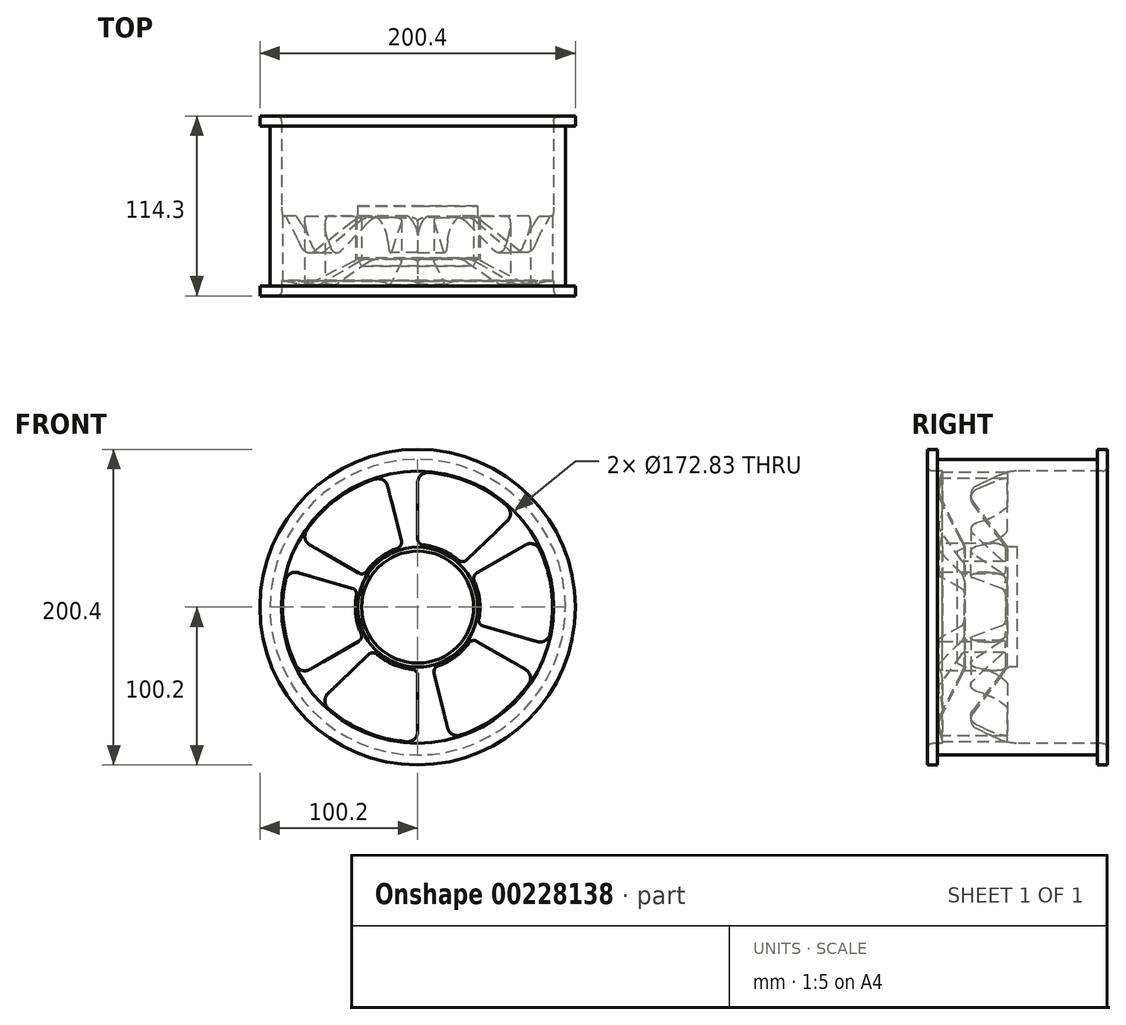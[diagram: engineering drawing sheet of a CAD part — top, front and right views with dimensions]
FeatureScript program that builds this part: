
annotation { "Feature Type Name" : "Feature", "Feature Type Description" : "" }
export const myFeature = defineFeature(function(context is Context, id is Id, definition is map)
    precondition{}
    {
        {
            var Q0;
            Q0=qCreatedBy(makeId("Right.planeOp"),FACE);
            var sketch = newSketch(context, id + "F0", { "sketchPlane" : qUnion([Q0])});
            skLineSegment(sketch, "E0", {"start": v(0, 0) * mm, "end": v(33.02, 0) * mm});
            skLineSegment(sketch, "E1", {"start": v(33.02, 0) * mm, "end": v(33.02, 38.1) * mm});
            skLineSegment(sketch, "E2", {"start": v(33.02, 38.1) * mm, "end": v(27.46, 38.1) * mm});
            skLineSegment(sketch, "E3", {"start": v(26.2, 38.73) * mm, "end": v(4.65, 67.46) * mm});
            skLineSegment(sketch, "E4", {"start": v(6.99, 77) * mm, "end": v(21.47, 83.93) * mm});
            skLineSegment(sketch, "E5", {"start": v(32.43, 86.42) * mm, "end": v(87, 86.42) * mm});
            skLineSegment(sketch, "E6", {"start": v(90.17, 89.6) * mm, "end": v(90.17, 100.2) * mm});
            skLineSegment(sketch, "E7", {"start": v(90.17, 100.2) * mm, "end": v(83.82, 100.2) * mm});
            skLineSegment(sketch, "E8", {"start": v(83.82, 100.2) * mm, "end": v(83.82, 93.85) * mm});
            skLineSegment(sketch, "E9", {"start": v(83.82, 93.85) * mm, "end": v(-17.78, 93.85) * mm});
            skLineSegment(sketch, "E10", {"start": v(-17.78, 93.85) * mm, "end": v(-17.78, 100.2) * mm});
            skLineSegment(sketch, "E11", {"start": v(-17.78, 100.2) * mm, "end": v(-24.13, 100.2) * mm});
            skLineSegment(sketch, "E12", {"start": v(-24.13, 100.2) * mm, "end": v(-24.13, 89.6) * mm});
            skLineSegment(sketch, "E13", {"start": v(-20.95, 86.42) * mm, "end": v(-14.5, 86.42) * mm});
            skLineSegment(sketch, "E14", {"start": v(-14.5, 86.42) * mm, "end": v(-16.6, 78.26) * mm});
            skLineSegment(sketch, "E15", {"start": v(-15.66, 69.41) * mm, "end": v(0, 38.1) * mm});
            skLineSegment(sketch, "E16", {"start": v(0, 38.1) * mm, "end": v(-5.08, 35.56) * mm});
            skLineSegment(sketch, "E17", {"start": v(-5.08, 35.56) * mm, "end": v(-5.08, 0) * mm});
            skLineSegment(sketch, "E18", {"start": v(-5.08, 0) * mm, "end": v(0, 0) * mm});
            skPoint(sketch, "E19.visualSharp", {"position": v(0, 73.66) * mm});
            skArc(sketch, "E19.filletArc", {"start": v(6.99, 77) * mm, "mid": v(3.56, 72.79) * mm, "end": v(4.65, 67.46) * mm});
            skPoint(sketch, "E20.visualSharp", {"position": v(26.67, 86.42) * mm});
            skArc(sketch, "E20.filletArc", {"start": v(32.43, 86.42) * mm, "mid": v(26.81, 85.79) * mm, "end": v(21.47, 83.93) * mm});
            skPoint(sketch, "E21.visualSharp", {"position": v(-17.78, 73.66) * mm});
            skArc(sketch, "E21.filletArc", {"start": v(-16.6, 78.26) * mm, "mid": v(-16.92, 73.75) * mm, "end": v(-15.66, 69.41) * mm});
            skPoint(sketch, "E22.visualSharp", {"position": v(90.17, 86.42) * mm});
            skArc(sketch, "E22.filletArc", {"start": v(87, 86.42) * mm, "mid": v(89.24, 87.35) * mm, "end": v(90.17, 89.6) * mm});
            skPoint(sketch, "E23.visualSharp", {"position": v(-24.13, 86.42) * mm});
            skArc(sketch, "E23.filletArc", {"start": v(-24.13, 89.6) * mm, "mid": v(-23.2, 87.35) * mm, "end": v(-20.95, 86.42) * mm});
            skPoint(sketch, "E24.visualSharp", {"position": v(26.67, 38.1) * mm});
            skArc(sketch, "E24.filletArc", {"start": v(26.2, 38.73) * mm, "mid": v(26.75, 38.27) * mm, "end": v(27.46, 38.1) * mm});
            skSolve(sketch);
        }
        {
            var Q0;
            Q0=makeQuery(id+"F0.imprint","IMPRINT",FACE,{"disambiguationData":[TD([[makeQuery(id+"F0.imprint","IMPRINT",EDGE,{"derivedFrom":sQuery(id+"F0.wireOp",EDGE,"E0")}),1.0]])]});
            var Q1;
            Q1=sQuery(id+"F0.wireOp",EDGE,"E0");
            revolve(context, id + "F1", {"entities" : qUnion([Q0]), "axis" : qUnion([Q1]), "revolveType" : RevolveType.FULL});
        }
        {
            var Q0;
            Q0=makeQuery(id+"F1.opRevolve","SWEPT_FACE",FACE,{"disambiguationData":[OSD([sQuery(id+"F0.wireOp",EDGE,"E17")])]});
            var sketch = newSketch(context, id + "F2", { "sketchPlane" : qUnion([Q0])});
            skArc(sketch, "E25", {"start": v(56.8, 64.21) * mm, "mid": v(33.55, 78.89) * mm, "end": v(6.86, 85.45) * mm});
            skArc(sketch, "E26", {"start": v(25.97, 29.83) * mm, "mid": v(15.47, 36.43) * mm, "end": v(3.45, 39.5) * mm});
            skLineSegment(sketch, "E27", {"start": v(0, 43.29) * mm, "end": v(0, 79.12) * mm});
            skLineSegment(sketch, "E28", {"start": v(31.11, 29.96) * mm, "end": v(57, 54.88) * mm});
            skLineSegment(sketch, "E29.1.0", {"start": v(-10.4, 41.93) * mm, "end": v(-19.04, 76.8) * mm});
            skArc(sketch, "E29.1.1", {"start": v(-12.85, 37.4) * mm, "mid": v(-23.81, 31.6) * mm, "end": v(-32.48, 22.74) * mm});
            skLineSegment(sketch, "E29.1.2", {"start": v(-37.49, 21.64) * mm, "end": v(-68.52, 39.56) * mm});
            skLineSegment(sketch, "E29.2.0", {"start": v(-41.5, 11.96) * mm, "end": v(-76.03, 21.91) * mm});
            skArc(sketch, "E29.2.1", {"start": v(-38.82, 7.57) * mm, "mid": v(-39.28, -4.82) * mm, "end": v(-35.93, -16.76) * mm});
            skLineSegment(sketch, "E29.2.2", {"start": v(-37.49, -21.64) * mm, "end": v(-68.52, -39.56) * mm});
            skLineSegment(sketch, "E29.3.0", {"start": v(-31.11, -29.96) * mm, "end": v(-57, -54.88) * mm});
            skArc(sketch, "E29.3.1", {"start": v(-25.97, -29.83) * mm, "mid": v(-15.47, -36.43) * mm, "end": v(-3.45, -39.5) * mm});
            skLineSegment(sketch, "E29.3.2", {"start": v(0, -43.29) * mm, "end": v(0, -79.12) * mm});
            skLineSegment(sketch, "E29.4.0", {"start": v(10.4, -41.93) * mm, "end": v(19.04, -76.8) * mm});
            skArc(sketch, "E29.4.1", {"start": v(12.85, -37.4) * mm, "mid": v(23.81, -31.6) * mm, "end": v(32.48, -22.74) * mm});
            skLineSegment(sketch, "E29.4.2", {"start": v(37.49, -21.64) * mm, "end": v(68.52, -39.56) * mm});
            skLineSegment(sketch, "E29.5.0", {"start": v(41.5, -11.96) * mm, "end": v(76.03, -21.91) * mm});
            skArc(sketch, "E29.5.1", {"start": v(38.82, -7.57) * mm, "mid": v(39.28, 4.82) * mm, "end": v(35.93, 16.76) * mm});
            skLineSegment(sketch, "E29.5.2", {"start": v(37.49, 21.64) * mm, "end": v(68.52, 39.56) * mm});
            skArc(sketch, "E30.trimOffspring", {"start": v(-27.21, 81.3) * mm, "mid": v(-51.54, 68.5) * mm, "end": v(-70.57, 48.66) * mm});
            skArc(sketch, "E31.trimOffspring", {"start": v(-84, 17.08) * mm, "mid": v(-85.1, -10.39) * mm, "end": v(-77.43, -36.79) * mm});
            skArc(sketch, "E32.trimOffspring", {"start": v(-56.8, -64.21) * mm, "mid": v(-33.55, -78.89) * mm, "end": v(-6.86, -85.45) * mm});
            skArc(sketch, "E33.trimOffspring", {"start": v(84, -17.08) * mm, "mid": v(85.1, 10.39) * mm, "end": v(77.43, 36.79) * mm});
            skArc(sketch, "E34.trimOffspring", {"start": v(27.21, -81.3) * mm, "mid": v(51.54, -68.5) * mm, "end": v(70.57, -48.66) * mm});
            skPoint(sketch, "E35.visualSharp", {"position": v(-38, 10.96) * mm});
            skArc(sketch, "E35.filletArc", {"start": v(-38.82, 7.57) * mm, "mid": v(-39.31, 10.3) * mm, "end": v(-41.5, 11.96) * mm});
            skPoint(sketch, "E36.visualSharp", {"position": v(-34.36, -19.84) * mm});
            skArc(sketch, "E36.filletArc", {"start": v(-37.49, -21.64) * mm, "mid": v(-35.76, -19.5) * mm, "end": v(-35.93, -16.76) * mm});
            skPoint(sketch, "E37.visualSharp", {"position": v(-28.5, -27.44) * mm});
            skArc(sketch, "E37.filletArc", {"start": v(-25.97, -29.83) * mm, "mid": v(-28.57, -28.9) * mm, "end": v(-31.11, -29.96) * mm});
            skPoint(sketch, "E38.visualSharp", {"position": v(0, -39.67) * mm});
            skArc(sketch, "E38.filletArc", {"start": v(0, -43.29) * mm, "mid": v(-1, -40.72) * mm, "end": v(-3.45, -39.5) * mm});
            skPoint(sketch, "E39.visualSharp", {"position": v(9.52, -38.4) * mm});
            skArc(sketch, "E39.filletArc", {"start": v(12.85, -37.4) * mm, "mid": v(10.74, -39.19) * mm, "end": v(10.4, -41.93) * mm});
            skPoint(sketch, "E40.visualSharp", {"position": v(34.36, -19.84) * mm});
            skArc(sketch, "E40.filletArc", {"start": v(37.49, -21.64) * mm, "mid": v(34.77, -21.22) * mm, "end": v(32.48, -22.74) * mm});
            skPoint(sketch, "E41.visualSharp", {"position": v(38, -10.96) * mm});
            skArc(sketch, "E41.filletArc", {"start": v(38.82, -7.57) * mm, "mid": v(39.31, -10.3) * mm, "end": v(41.5, -11.96) * mm});
            skPoint(sketch, "E42.visualSharp", {"position": v(34.36, 19.84) * mm});
            skArc(sketch, "E42.filletArc", {"start": v(37.49, 21.64) * mm, "mid": v(35.76, 19.5) * mm, "end": v(35.93, 16.76) * mm});
            skPoint(sketch, "E43.visualSharp", {"position": v(28.5, 27.44) * mm});
            skArc(sketch, "E43.filletArc", {"start": v(25.97, 29.83) * mm, "mid": v(28.57, 28.9) * mm, "end": v(31.11, 29.96) * mm});
            skPoint(sketch, "E44.visualSharp", {"position": v(0, 39.67) * mm});
            skArc(sketch, "E44.filletArc", {"start": v(0, 43.29) * mm, "mid": v(1, 40.72) * mm, "end": v(3.45, 39.5) * mm});
            skPoint(sketch, "E45.visualSharp", {"position": v(-9.52, 38.4) * mm});
            skArc(sketch, "E45.filletArc", {"start": v(-12.85, 37.4) * mm, "mid": v(-10.74, 39.19) * mm, "end": v(-10.4, 41.93) * mm});
            skPoint(sketch, "E46.visualSharp", {"position": v(-34.36, 19.84) * mm});
            skArc(sketch, "E46.filletArc", {"start": v(-37.49, 21.64) * mm, "mid": v(-34.77, 21.22) * mm, "end": v(-32.48, 22.74) * mm});
            skPoint(sketch, "E47.visualSharp", {"position": v(20.62, -83.2) * mm});
            skArc(sketch, "E47.filletArc", {"start": v(19.04, -76.8) * mm, "mid": v(22.14, -80.83) * mm, "end": v(27.21, -81.3) * mm});
            skPoint(sketch, "E48.visualSharp", {"position": v(74.24, -42.86) * mm});
            skArc(sketch, "E48.filletArc", {"start": v(70.57, -48.66) * mm, "mid": v(71.54, -43.66) * mm, "end": v(68.52, -39.56) * mm});
            skPoint(sketch, "E49.visualSharp", {"position": v(82.37, -23.74) * mm});
            skArc(sketch, "E49.filletArc", {"start": v(76.03, -21.91) * mm, "mid": v(81.08, -21.24) * mm, "end": v(84, -17.08) * mm});
            skPoint(sketch, "E50.visualSharp", {"position": v(74.24, 42.86) * mm});
            skArc(sketch, "E50.filletArc", {"start": v(77.43, 36.79) * mm, "mid": v(73.58, 40.12) * mm, "end": v(68.52, 39.56) * mm});
            skPoint(sketch, "E51.visualSharp", {"position": v(61.75, 59.46) * mm});
            skArc(sketch, "E51.filletArc", {"start": v(57, 54.88) * mm, "mid": v(58.93, 59.6) * mm, "end": v(56.8, 64.21) * mm});
            skPoint(sketch, "E52.visualSharp", {"position": v(0, 85.73) * mm});
            skArc(sketch, "E52.filletArc", {"start": v(6.86, 85.45) * mm, "mid": v(2.04, 83.79) * mm, "end": v(0, 79.12) * mm});
            skPoint(sketch, "E53.visualSharp", {"position": v(-20.62, 83.2) * mm});
            skArc(sketch, "E53.filletArc", {"start": v(-19.04, 76.8) * mm, "mid": v(-22.14, 80.83) * mm, "end": v(-27.21, 81.3) * mm});
            skPoint(sketch, "E54.visualSharp", {"position": v(-74.24, 42.86) * mm});
            skArc(sketch, "E54.filletArc", {"start": v(-70.57, 48.66) * mm, "mid": v(-71.54, 43.66) * mm, "end": v(-68.52, 39.56) * mm});
            skPoint(sketch, "E55.visualSharp", {"position": v(-82.37, 23.74) * mm});
            skArc(sketch, "E55.filletArc", {"start": v(-76.03, 21.91) * mm, "mid": v(-81.08, 21.24) * mm, "end": v(-84, 17.08) * mm});
            skPoint(sketch, "E56.visualSharp", {"position": v(-74.24, -42.86) * mm});
            skArc(sketch, "E56.filletArc", {"start": v(-77.43, -36.79) * mm, "mid": v(-73.58, -40.12) * mm, "end": v(-68.52, -39.56) * mm});
            skPoint(sketch, "E57.visualSharp", {"position": v(-61.75, -59.46) * mm});
            skArc(sketch, "E57.filletArc", {"start": v(-57, -54.88) * mm, "mid": v(-58.93, -59.6) * mm, "end": v(-56.8, -64.21) * mm});
            skPoint(sketch, "E58.visualSharp", {"position": v(0, -85.73) * mm});
            skArc(sketch, "E58.filletArc", {"start": v(-6.86, -85.45) * mm, "mid": v(-2.04, -83.79) * mm, "end": v(0, -79.12) * mm});
            skSolve(sketch);
        }
        {
            var Q0;
            Q0 = qSketchRegion(id + "F2", true);
            extrude(context, id + "F3", {"entities" : qUnion([Q0]), "operationType" : NewBodyOperationType.REMOVE, "endBound" : BoundingType.THROUGH_ALL, "oppositeDirection" : true, "depth" : 25.4 * mm, "hasSecondDirection" : true, "secondDirectionBound" : SecondDirectionBoundingType.THROUGH_ALL, "secondDirectionOppositeDirection" : false, "secondDirectionDepth" : 25.4 * mm});
        }
    });
